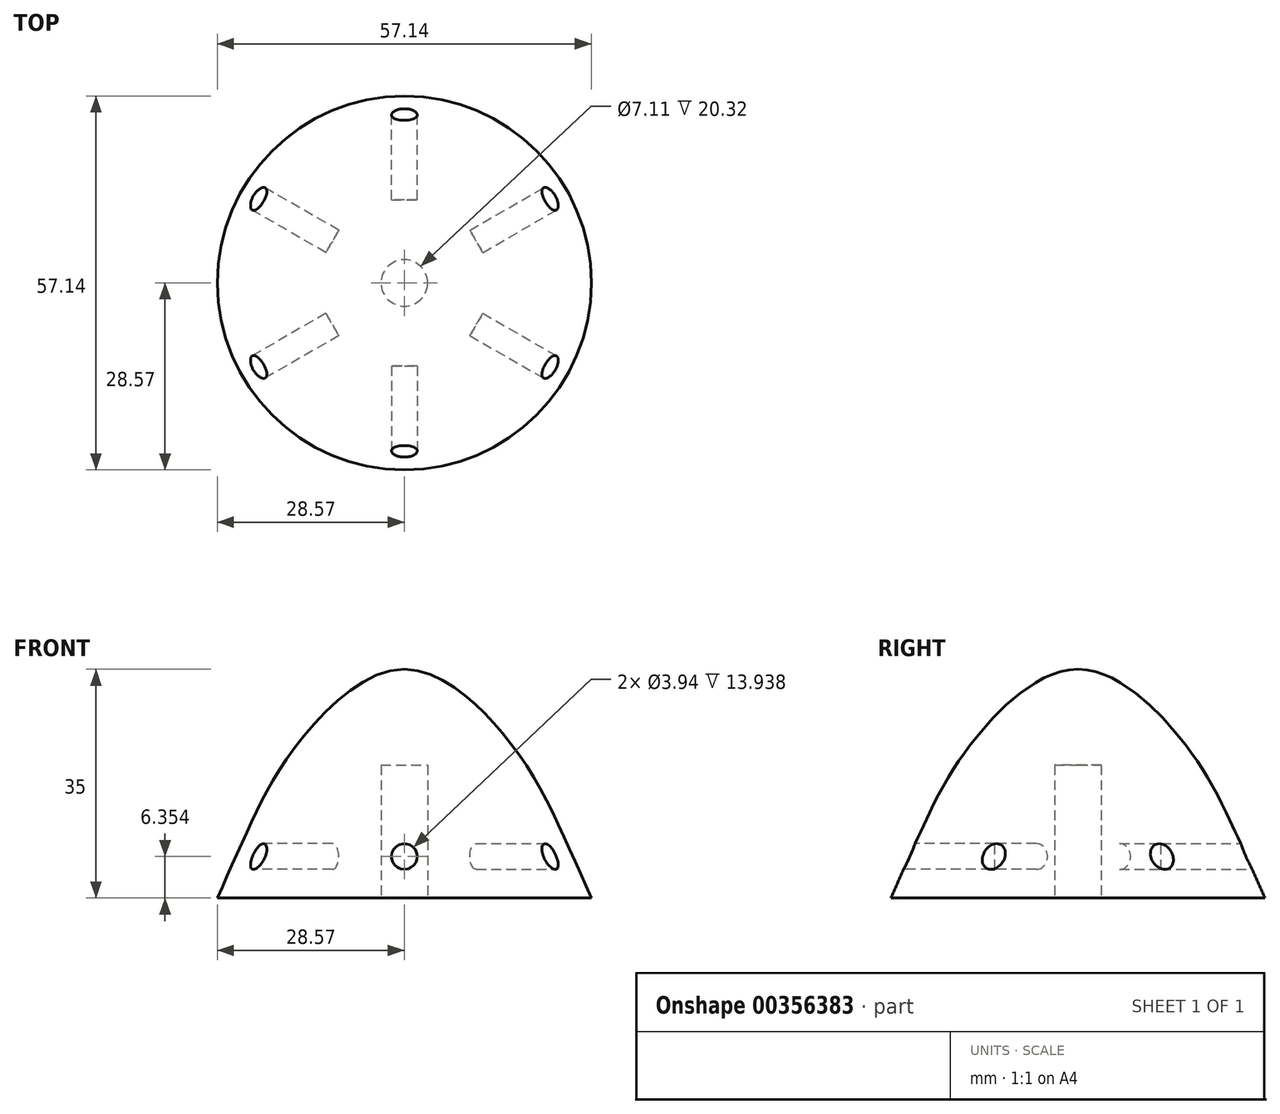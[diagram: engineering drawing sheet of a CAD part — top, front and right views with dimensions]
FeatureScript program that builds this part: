
annotation { "Feature Type Name" : "Feature", "Feature Type Description" : "" }
export const myFeature = defineFeature(function(context is Context, id is Id, definition is map)
    precondition{}
    {
        {
            var Q0;
            Q0=qCreatedBy(makeId("Front.planeOp"),FACE);
            var sketch = newSketch(context, id + "F0", { "sketchPlane" : qUnion([Q0])});
            skPoint(sketch, "E0", {"position": v(0, 12.41) * mm});
            skPoint(sketch, "E1", {"position": v(0, 14.95) * mm});
            skLineSegment(sketch, "E2", {"start": v(-16.86, 17.5) * mm, "end": v(15.78, 17.5) * mm});
            skFitSpline(sketch, "E3", {"points": [v(-12.44, -0.29) * mm, v(-10.16, 4.8) * mm, v(-7.18, 9.87) * mm, v(0, 14.95) * mm, v(7.18, 9.87) * mm, v(10.16, 4.8) * mm, v(12.44, -0.29) * mm], "startDerivative": vector(15.04, 34.12) * mm, "endDerivative": vector(15.04, -34.12) * mm});
            skLineSegment(sketch, "E4", {"start": v(-12.44, -0.29) * mm, "end": v(12.44, -0.29) * mm});
            skLineSegment(sketch, "E5", {"start": v(0, -0.29) * mm, "end": v(0, 14.95) * mm});
            skSolve(sketch);
        }
        {
            var Q0;
            {var subQ3=sQuery(id+"F0.wireOp",EDGE,"E5");Q0=makeQuery(id+"F0.imprint","IMPRINT",FACE,{"disambiguationData":[TD([[makeQuery(id+"F0.imprint","IMPRINT",EDGE,{"derivedFrom":subQ3}),1.0]])]});}
            var Q1;
            Q1=sQuery(id+"F0.wireOp",EDGE,"E5");
            revolve(context, id + "F1", {"surfaceOperationType" : NewSurfaceOperationType.NEW, "entities" : qUnion([Q0]), "axis" : qUnion([Q1]), "revolveType" : RevolveType.ONE_DIRECTION, "angle" : 360 * degree});
        }
        {
            var Q0;
            Q0=makeQuery(id+"F1.opRevolve","SWEPT_BODY",BODY,{"disambiguationData":[OSD([sQuery(id+"F0.wireOp",EDGE,"E3"),sQuery(id+"F0.wireOp",EDGE,"E4"),sQuery(id+"F0.wireOp",EDGE,"E5")])]});
            var Q1;
            Q1=qCreatedBy(makeId("Origin.pointOp"),VERTEX);
            var Q2;
            Q2=qCreatedBy(makeId("Origin.pointOp"),VERTEX);
            transform(context, id + "F2", {"entities" : qUnion([Q0]), "transformType" : TransformType.SCALE_UNIFORMLY, "scale" : 1.79, "scalePoint" : qUnion([Q2]), "makeCopy" : false});
        }
        {
            var Q0;
            Q0=makeQuery(id+"F1.opRevolve","SWEPT_BODY",BODY,{"disambiguationData":[OSD([sQuery(id+"F0.wireOp",EDGE,"E3"),sQuery(id+"F0.wireOp",EDGE,"E4"),sQuery(id+"F0.wireOp",EDGE,"E5")])]});
            var Q1;
            Q1=qCreatedBy(makeId("Origin.pointOp"),VERTEX);
            transform(context, id + "F3", {"entities" : qUnion([Q0]), "transformType" : TransformType.SCALE_UNIFORMLY, "scale" : 1.29, "scalePoint" : qUnion([Q1]), "makeCopy" : false});
        }
        {
            var Q0;
            Q0=makeQuery(id+"F1.opRevolve","SWEPT_FACE",FACE,{"disambiguationData":[OSD([sQuery(id+"F0.wireOp",EDGE,"E4")])]});
            var sketch = newSketch(context, id + "F4", { "sketchPlane" : qUnion([Q0])});
            skLineSegment(sketch, "E6", {"start": v(0, 0) * mm, "end": v(-14.29, 24.75) * mm});
            skLineSegment(sketch, "E7", {"start": v(-14.29, 24.75) * mm, "end": v(14.29, 24.75) * mm});
            skLineSegment(sketch, "E8", {"start": v(14.29, 24.75) * mm, "end": v(0, 0) * mm});
            skSolve(sketch);
        }
        {
            var Q0;
            {var subQ0=sQuery(id+"F4.wireOp",EDGE,"E6");Q0=makeQuery(id+"F4.imprint","IMPRINT",FACE,{"disambiguationData":[TD([[makeQuery(id+"F4.imprint","IMPRINT",EDGE,{"derivedFrom":subQ0}),1.0]])]});}
            extrude(context, id + "F5", {"entities" : qUnion([Q0]), "operationType" : NewBodyOperationType.REMOVE, "oppositeDirection" : true, "depth" : 127 * mm, "offsetDistance" : 25.4 * mm});
        }
        {
            var Q0;
            Q0=qCreatedBy(makeId("Front.planeOp"),FACE);
            cPlane(context, id + "F6", {"entities" : qUnion([Q0]), "cplaneType" : CPlaneType.OFFSET, "offset" : 38.1 * mm, "width" : 152.4 * mm, "height" : 152.4 * mm});
        }
        {
            var Q0;
            Q0=qCreatedBy(id+"F6.planeOp",FACE);
            var sketch = newSketch(context, id + "F7", { "sketchPlane" : qUnion([Q0])});
            skCircle(sketch, "E9", {"center": v(0, 5.7) * mm, "radius": 1.97 * mm});
            skSolve(sketch);
        }
        {
            var Q0;
            Q0=makeQuery(id+"F7.imprint","IMPRINT",FACE,{"disambiguationData":[TD([[makeQuery(id+"F7.imprint","IMPRINT",EDGE,{"derivedFrom":sQuery(id+"F7.wireOp",EDGE,"E9")}),1.0]])]});
            extrude(context, id + "F8", {"entities" : qUnion([Q0]), "operationType" : NewBodyOperationType.REMOVE, "oppositeDirection" : true, "depth" : 25.4 * mm, "offsetDistance" : 25.4 * mm});
        }
        {
            var Q0;
            Q0=qCreatedBy(makeId("Front.planeOp"),FACE);
            var sketch = newSketch(context, id + "F9", { "sketchPlane" : qUnion([Q0])});
            skLineSegment(sketch, "E10", {"start": v(0, 0) * mm, "end": v(0, 46.2) * mm});
            skSolve(sketch);
        }
        {
            var Q0;
            Q0=makeQuery(id+"F1.opRevolve","SWEPT_BODY",BODY,{"disambiguationData":[OSD([sQuery(id+"F0.wireOp",EDGE,"E3"),sQuery(id+"F0.wireOp",EDGE,"E4"),sQuery(id+"F0.wireOp",EDGE,"E5")])]});
            var Q1;
            Q1=sQuery(id+"F9.wireOp",EDGE,"E10");
            circularPattern(context, id + "F10", {"entities" : qUnion([Q0]), "axis" : qUnion([Q1]), "angle" : 360 * degree, "instanceCount" : 6, "equalSpace" : true});
        }
        {
            var Q0;
            Q0=makeQuery(id+"F1.opRevolve","SWEPT_BODY",BODY,{"disambiguationData":[OSD([sQuery(id+"F0.wireOp",EDGE,"E3"),sQuery(id+"F0.wireOp",EDGE,"E4"),sQuery(id+"F0.wireOp",EDGE,"E5")])]});
            var Q1;
            Q1=makeQuery(id+"F10.opPattern","COPY",BODY,{"derivedFrom":makeQuery(id+"F1.opRevolve","SWEPT_BODY",BODY,{"disambiguationData":[OSD([sQuery(id+"F0.wireOp",EDGE,"E3"),sQuery(id+"F0.wireOp",EDGE,"E4"),sQuery(id+"F0.wireOp",EDGE,"E5")])]}),"instanceName":"2"});
            var Q2;
            Q2=makeQuery(id+"F10.opPattern","COPY",BODY,{"derivedFrom":makeQuery(id+"F1.opRevolve","SWEPT_BODY",BODY,{"disambiguationData":[OSD([sQuery(id+"F0.wireOp",EDGE,"E3"),sQuery(id+"F0.wireOp",EDGE,"E4"),sQuery(id+"F0.wireOp",EDGE,"E5")])]}),"instanceName":"1"});
            var Q3;
            Q3=makeQuery(id+"F10.opPattern","COPY",BODY,{"derivedFrom":makeQuery(id+"F1.opRevolve","SWEPT_BODY",BODY,{"disambiguationData":[OSD([sQuery(id+"F0.wireOp",EDGE,"E3"),sQuery(id+"F0.wireOp",EDGE,"E4"),sQuery(id+"F0.wireOp",EDGE,"E5")])]}),"instanceName":"5"});
            var Q4;
            Q4=makeQuery(id+"F10.opPattern","COPY",BODY,{"derivedFrom":makeQuery(id+"F1.opRevolve","SWEPT_BODY",BODY,{"disambiguationData":[OSD([sQuery(id+"F0.wireOp",EDGE,"E3"),sQuery(id+"F0.wireOp",EDGE,"E4"),sQuery(id+"F0.wireOp",EDGE,"E5")])]}),"instanceName":"3"});
            var Q5;
            Q5=makeQuery(id+"F10.opPattern","COPY",BODY,{"derivedFrom":makeQuery(id+"F1.opRevolve","SWEPT_BODY",BODY,{"disambiguationData":[OSD([sQuery(id+"F0.wireOp",EDGE,"E3"),sQuery(id+"F0.wireOp",EDGE,"E4"),sQuery(id+"F0.wireOp",EDGE,"E5")])]}),"instanceName":"4"});
            booleanBodies(context, id + "F11", {"operationType" : BooleanOperationType.UNION, "tools" : qUnion([Q0, Q1, Q2, Q3, Q4, Q5])});
        }
        {
            var Q0;
            {var subQ0=makeQuery(id+"F1.opRevolve","SWEPT_FACE",FACE,{"disambiguationData":[OSD([sQuery(id+"F0.wireOp",EDGE,"E4")])]});Q0=makeQuery(id+"F11.opBoolean","MERGE",FACE,{"derivedFrom":[subQ0,makeQuery(id+"F10.opPattern","COPY",FACE,{"derivedFrom":subQ0,"instanceName":"1"}),makeQuery(id+"F10.opPattern","COPY",FACE,{"derivedFrom":subQ0,"instanceName":"2"}),makeQuery(id+"F10.opPattern","COPY",FACE,{"derivedFrom":subQ0,"instanceName":"3"}),makeQuery(id+"F10.opPattern","COPY",FACE,{"derivedFrom":subQ0,"instanceName":"4"}),makeQuery(id+"F10.opPattern","COPY",FACE,{"derivedFrom":subQ0,"instanceName":"5"})]});}
            var sketch = newSketch(context, id + "F12", { "sketchPlane" : qUnion([Q0])});
            skCircle(sketch, "E11", {"center": v(0, 0) * mm, "radius": 3.56 * mm});
            skSolve(sketch);
        }
        {
            var Q0;
            Q0=makeQuery(id+"F12.imprint","IMPRINT",FACE,{"disambiguationData":[TD([[makeQuery(id+"F12.imprint","IMPRINT",EDGE,{"derivedFrom":sQuery(id+"F12.wireOp",EDGE,"E11")}),1.0]])]});
            extrude(context, id + "F13", {"entities" : qUnion([Q0]), "operationType" : NewBodyOperationType.REMOVE, "oppositeDirection" : true, "depth" : 20.32 * mm, "offsetDistance" : 25.4 * mm});
        }
    });
